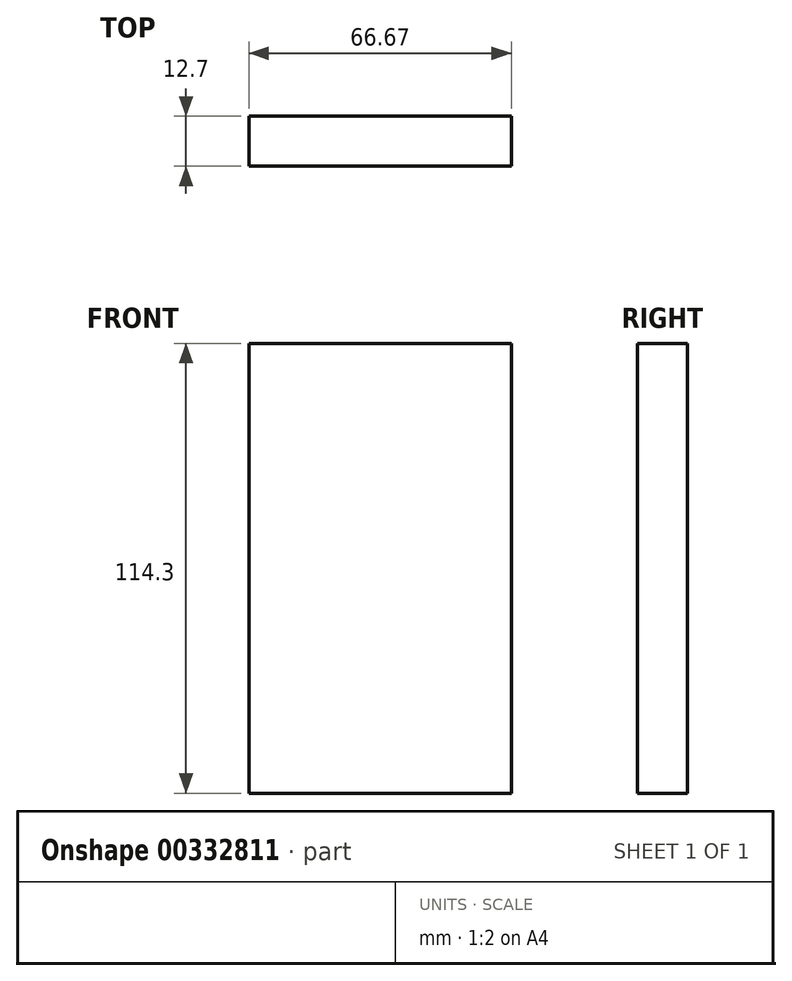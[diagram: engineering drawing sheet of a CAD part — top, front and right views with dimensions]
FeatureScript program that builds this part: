
annotation { "Feature Type Name" : "Feature", "Feature Type Description" : "" }
export const myFeature = defineFeature(function(context is Context, id is Id, definition is map)
    precondition{}
    {
        {
            var Q0;
            Q0=qCreatedBy(makeId("Front.planeOp"),FACE);
            var sketch = newSketch(context, id + "F0", { "sketchPlane" : qUnion([Q0])});
            skLineSegment(sketch, "E0.bottom", {"start": v(-65.5, 53.5) * mm, "end": v(1.18, 53.5) * mm});
            skLineSegment(sketch, "E0.top", {"start": v(-65.5, -60.8) * mm, "end": v(1.18, -60.8) * mm});
            skLineSegment(sketch, "E0.left", {"start": v(-65.5, 53.5) * mm, "end": v(-65.5, -60.8) * mm});
            skLineSegment(sketch, "E0.right", {"start": v(1.18, 53.5) * mm, "end": v(1.18, -60.8) * mm});
            skSolve(sketch);
        }
        {
            var Q0;
            Q0=makeQuery(id+"F0.imprint","IMPRINT",FACE,{"disambiguationData":[TD([[makeQuery(id+"F0.imprint","IMPRINT",EDGE,{"derivedFrom":sQuery(id+"F0.wireOp",EDGE,"E0.bottom")}),-1.0]])]});
            extrude(context, id + "F1", {"entities" : qUnion([Q0]), "depth" : 12.7 * mm});
        }
    });
